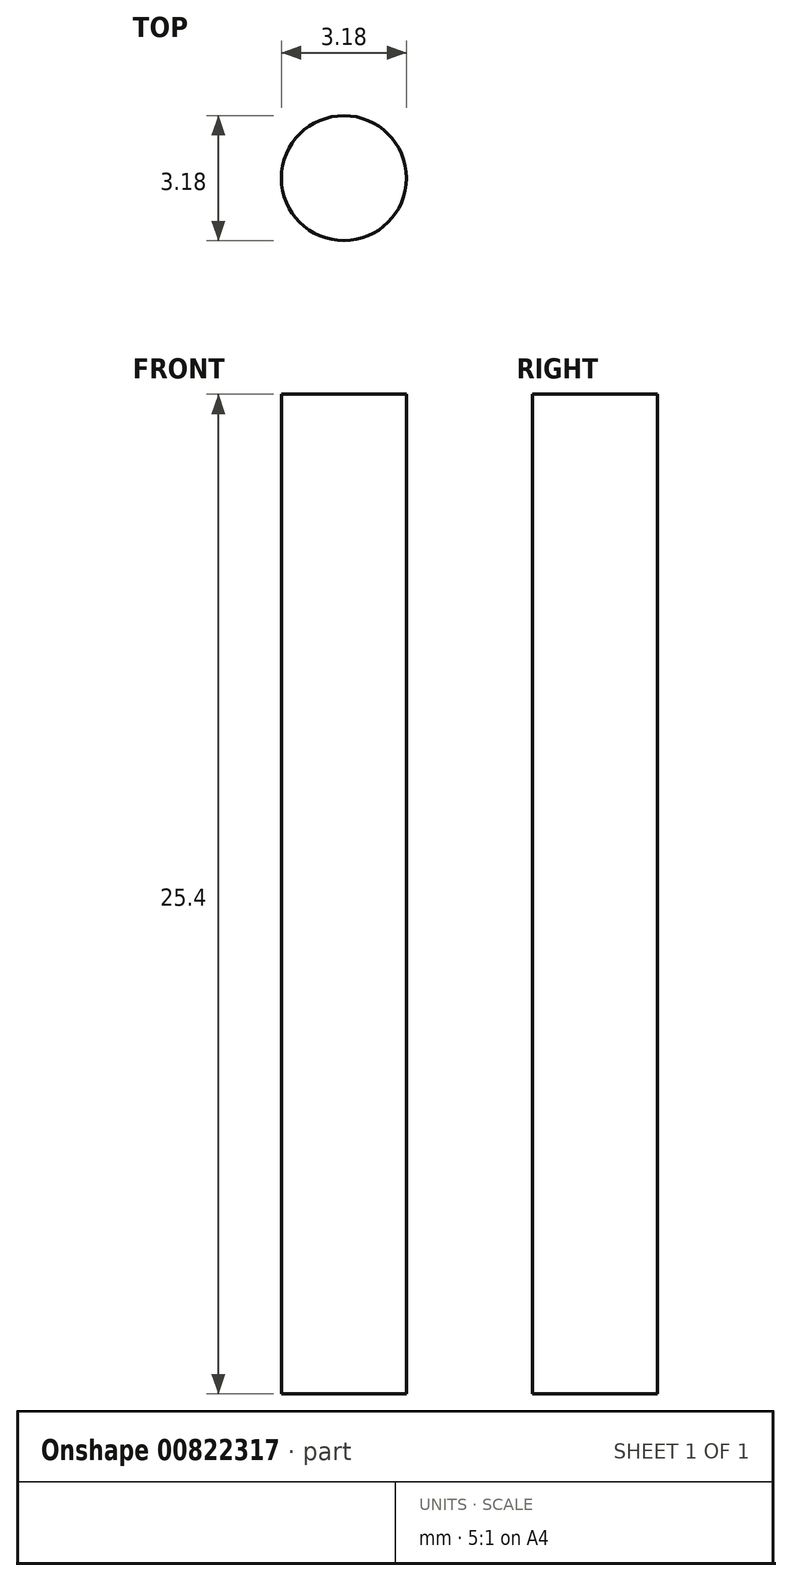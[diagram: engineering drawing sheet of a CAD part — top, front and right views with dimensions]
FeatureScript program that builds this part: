
annotation { "Feature Type Name" : "Feature", "Feature Type Description" : "" }
export const myFeature = defineFeature(function(context is Context, id is Id, definition is map)
    precondition{}
    {
        {
            var Q0;
            Q0=qCreatedBy(makeId("Top.planeOp"),FACE);
            var sketch = newSketch(context, id + "F0", { "sketchPlane" : qUnion([Q0])});
            skCircle(sketch, "E0", {"center": v(0, 0) * mm, "radius": 1.59 * mm});
            skSolve(sketch);
        }
        {
            var Q0;
            Q0=qSketchRegion(id+"F0",true);
            extrude(context, id + "F1", {"entities" : qUnion([Q0]), "depth" : 25.4 * mm, "offsetDistance" : 25.4 * mm});
        }
    });
